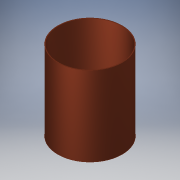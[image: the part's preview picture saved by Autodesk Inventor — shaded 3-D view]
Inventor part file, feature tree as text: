
AUTODESK INVENTOR PART (.ipt)
format: ipt  version: 2018 (Build 220112000, 112)  size: 100,352 bytes
history: native  units: in
note: dims shown in document units (in); Inventor stores cm internally (conversion verified against a paired STEP export)
features: extrude x1, sketch x1
ambient origin geometry x8: Origin, YZ Plane, XZ Plane, XY Plane, X Axis, Y Axis, Z Axis, Center Point
bodies: Solid1 (feature_tree)
feature tree (2):
  extrude  "Extrusion1"  Depth=9.875in
  sketch  "Sketch1"  dims[d0=8.0in d1=0.08in d2=9.875in d3=0.0in]
